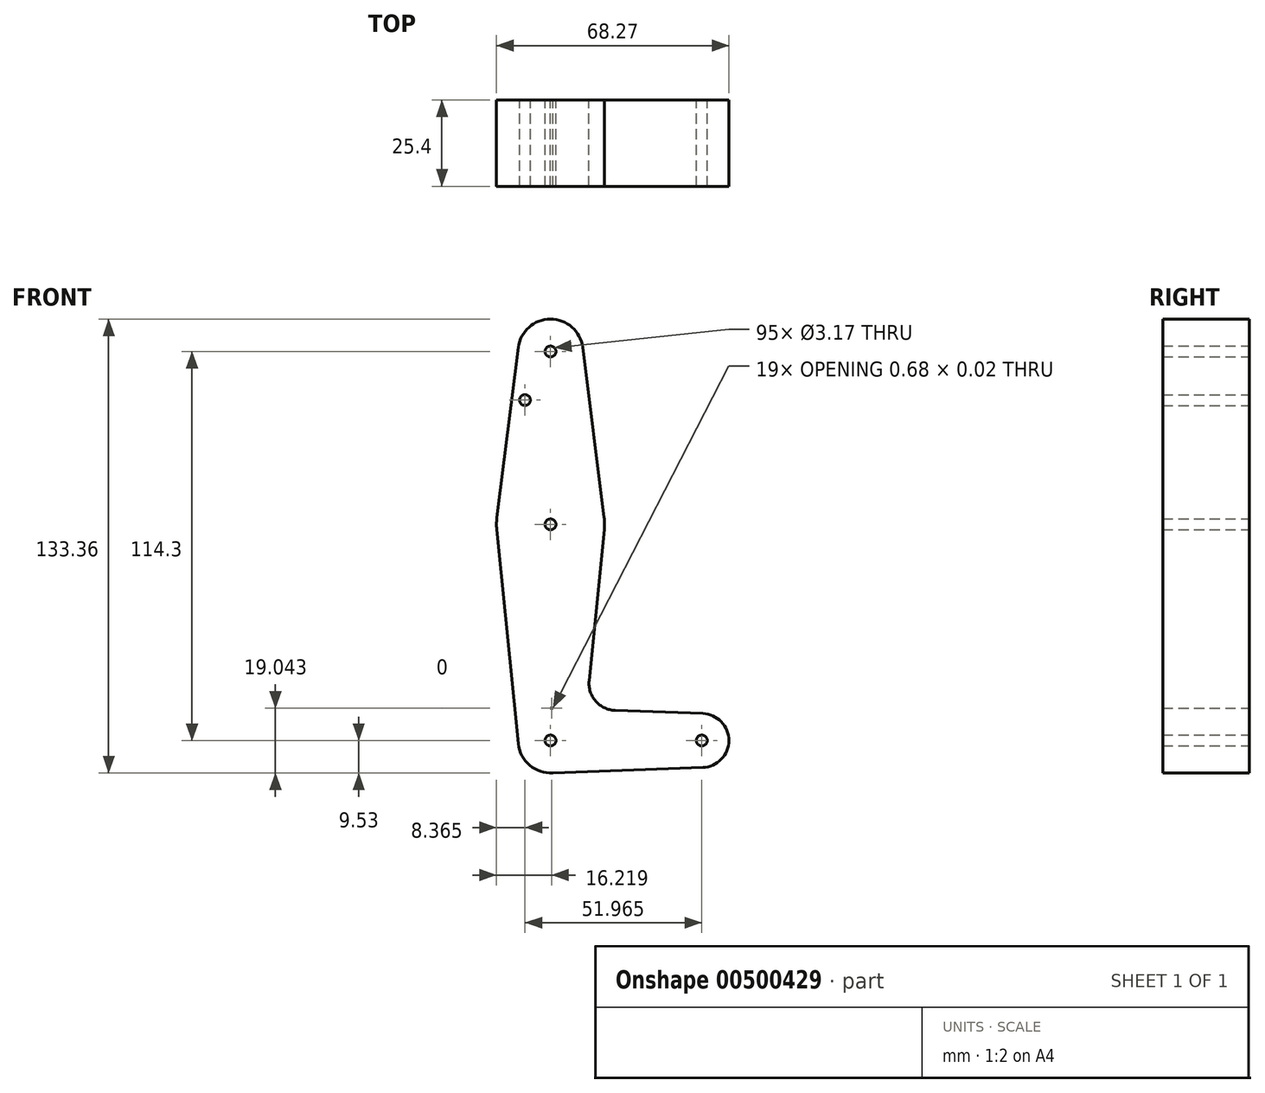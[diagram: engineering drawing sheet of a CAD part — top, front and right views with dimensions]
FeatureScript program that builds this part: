
annotation { "Feature Type Name" : "Feature", "Feature Type Description" : "" }
export const myFeature = defineFeature(function(context is Context, id is Id, definition is map)
    precondition{}
    {
        {
            var Q0;
            Q0=qCreatedBy(makeId("Front.planeOp"),FACE);
            var sketch = newSketch(context, id + "F0", { "sketchPlane" : qUnion([Q0])});
            skLineSegment(sketch, "E0", {"start": v(0, 114.3) * mm, "end": v(0, 0) * mm, "construction": true});
            skLineSegment(sketch, "E1", {"start": v(0, 0) * mm, "end": v(44.45, 0) * mm, "construction": true});
            skCircle(sketch, "E2", {"center": v(0, 114.3) * mm, "radius": 9.53 * mm});
            skCircle(sketch, "E3", {"center": v(0, 63.5) * mm, "radius": 15.88 * mm});
            skCircle(sketch, "E4", {"center": v(0, 0) * mm, "radius": 9.53 * mm});
            skCircle(sketch, "E5", {"center": v(44.45, 0) * mm, "radius": 7.94 * mm});
            skLineSegment(sketch, "E6", {"start": v(-9.45, 115.5) * mm, "end": v(-15.75, 65.48) * mm});
            skLineSegment(sketch, "E7", {"start": v(9.45, 115.5) * mm, "end": v(15.75, 65.48) * mm});
            skLineSegment(sketch, "E8", {"start": v(15.8, 61.91) * mm, "end": v(11.34, 17.59) * mm});
            skLineSegment(sketch, "E9", {"start": v(-15.8, 61.91) * mm, "end": v(-9.48, -0.95) * mm});
            skLineSegment(sketch, "E10", {"start": v(0, 9.53) * mm, "end": v(0.68, 9.5) * mm});
            skLineSegment(sketch, "E11", {"start": v(0, -9.53) * mm, "end": v(44.73, -7.93) * mm});
            skCircle(sketch, "E12", {"center": v(0, 114.3) * mm, "radius": 1.59 * mm});
            skCircle(sketch, "E13", {"center": v(-7.51, 100.03) * mm, "radius": 1.59 * mm});
            skCircle(sketch, "E14", {"center": v(0, 63.5) * mm, "radius": 1.59 * mm});
            skCircle(sketch, "E15", {"center": v(0, 0) * mm, "radius": 1.59 * mm});
            skCircle(sketch, "E16", {"center": v(44.45, 0) * mm, "radius": 1.59 * mm});
            skLineSegment(sketch, "E17.trimOffspring", {"start": v(18.97, 8.85) * mm, "end": v(44.73, 7.93) * mm});
            skLineSegment(sketch, "E18.trimOffspring", {"start": v(9.57, 0) * mm, "end": v(9.48, -0.95) * mm});
            skPoint(sketch, "E19.visualSharp", {"position": v(10.5, 9.15) * mm});
            skArc(sketch, "E19.filletArc", {"start": v(11.34, 17.59) * mm, "mid": v(13.26, 11.57) * mm, "end": v(18.97, 8.85) * mm});
            skSolve(sketch);
        }
        {
            var Q0;
            Q0 = qSketchRegion(id + "F0", true);
            extrude(context, id + "F1", {"entities" : qUnion([Q0]), "depth" : 25.4 * mm});
        }
    });
